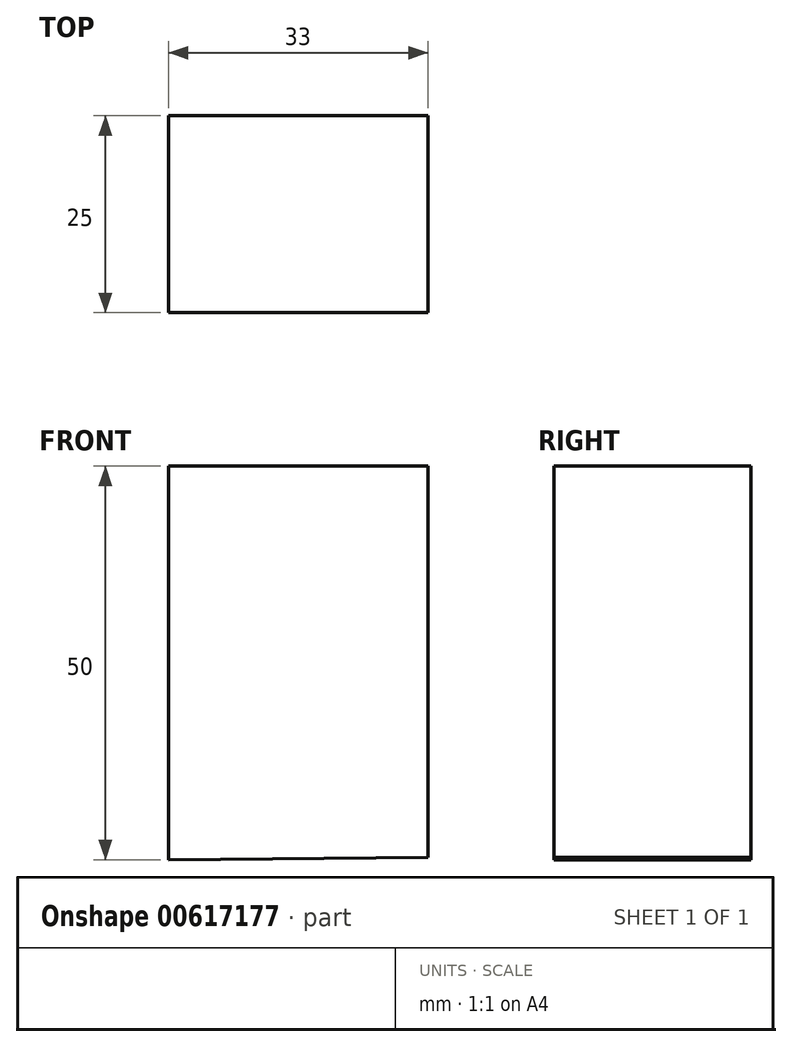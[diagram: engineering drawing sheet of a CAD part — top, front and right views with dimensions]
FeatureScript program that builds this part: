
annotation { "Feature Type Name" : "Feature", "Feature Type Description" : "" }
export const myFeature = defineFeature(function(context is Context, id is Id, definition is map)
    precondition{}
    {
        {
            var Q0;
            Q0=qCreatedBy(makeId("Front.planeOp"),FACE);
            var sketch = newSketch(context, id + "F0", { "sketchPlane" : qUnion([Q0])});
            skLineSegment(sketch, "E0", {"start": v(-53.55, 46.4) * mm, "end": v(-20.55, 46.4) * mm});
            skLineSegment(sketch, "E1", {"start": v(-53.55, 46.4) * mm, "end": v(-53.55, -3.6) * mm});
            skLineSegment(sketch, "E2", {"start": v(-20.55, 46.4) * mm, "end": v(-20.55, -3.3) * mm});
            skLineSegment(sketch, "E3", {"start": v(-53.55, -3.6) * mm, "end": v(-20.55, -3.3) * mm});
            skSolve(sketch);
        }
        {
            var Q0;
            Q0=makeQuery(id+"F0.imprint","IMPRINT",FACE,{"disambiguationData":[TD([[makeQuery(id+"F0.imprint","IMPRINT",EDGE,{"derivedFrom":sQuery(id+"F0.wireOp",EDGE,"E0")}),-1.0]])]});
            extrude(context, id + "F1", {"entities" : qUnion([Q0]), "depth" : 25 * mm, "offsetDistance" : 25 * mm});
        }
    });
